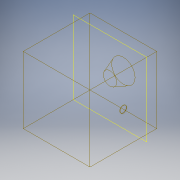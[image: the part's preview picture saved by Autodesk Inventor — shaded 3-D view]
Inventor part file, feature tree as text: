
AUTODESK INVENTOR PART (.ipt)
format: ipt  version: 2019.1 (Build 231200000, 200)  size: 137,728 bytes
history: native  units: mm
features: sketch x4, other x2, extrude x2, loft x1
ambient origin geometry x8: Origin, YZ Plane, XZ Plane, XY Plane, X Axis, Y Axis, Z Axis, Center Point
bodies: Body1 (feature_tree)
feature tree (9):
  other  "ソリッド1"
  extrude  "押し出し1"  Depth=2000.0mm
  sketch  "スケッチ2"
  other  "作業平面1"
  loft  "ロフト1"
  extrude  "押し出し2"  Depth=2000.0mm TaperAngle=0.0deg
  sketch  "スケッチ1"
  sketch  "スケッチ3"
  sketch  "スケッチ4"
